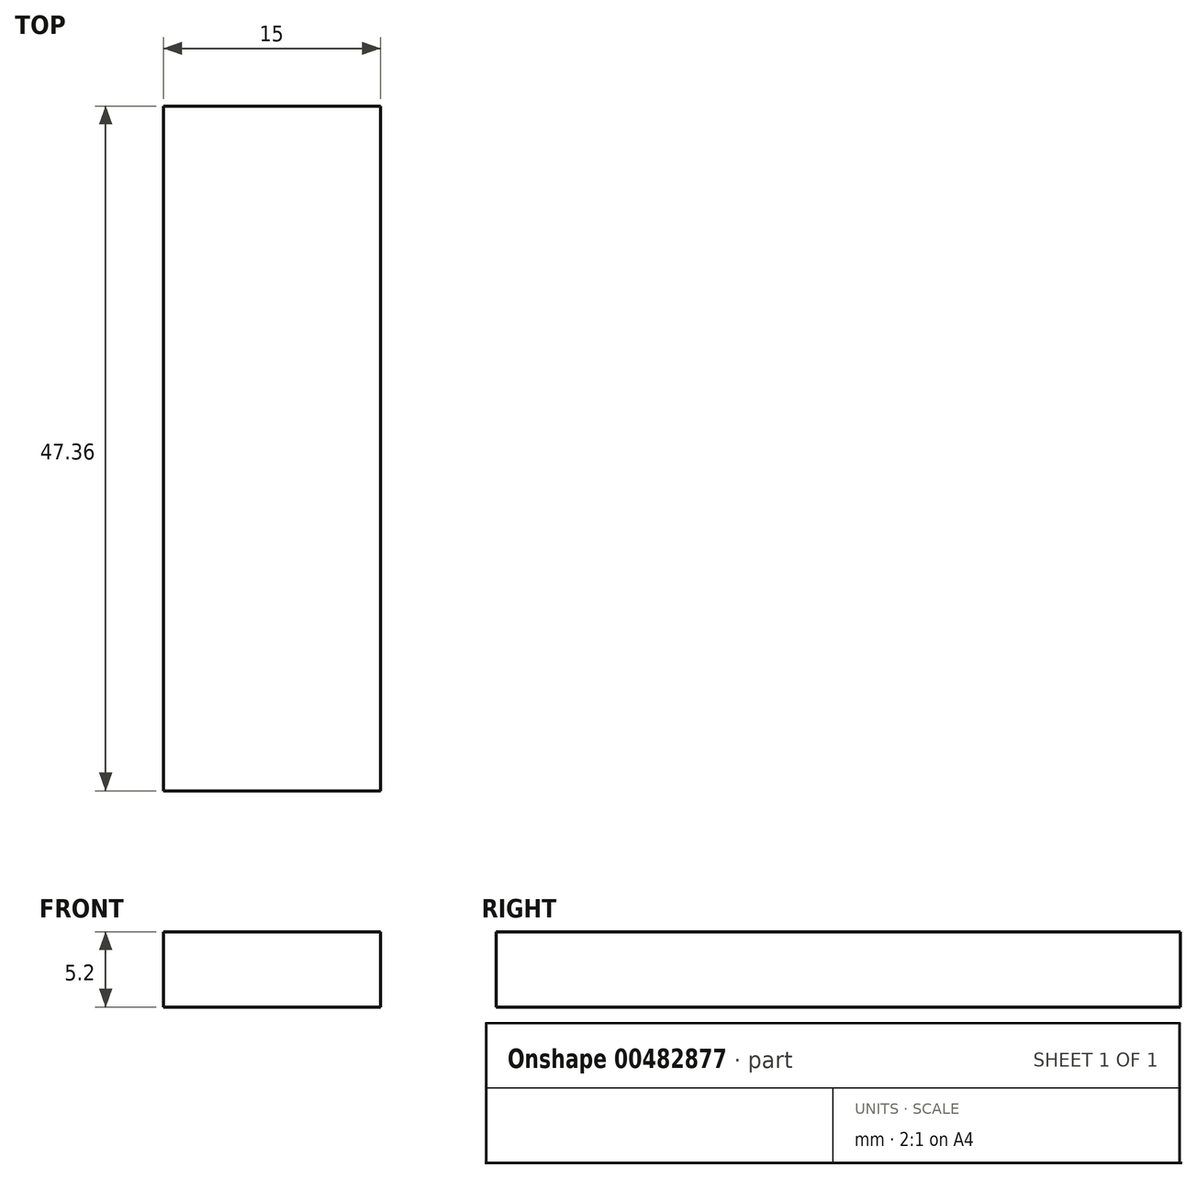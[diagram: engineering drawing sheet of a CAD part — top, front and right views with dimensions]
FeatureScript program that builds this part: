
annotation { "Feature Type Name" : "Feature", "Feature Type Description" : "" }
export const myFeature = defineFeature(function(context is Context, id is Id, definition is map)
    precondition{}
    {
        {
            var Q0;
            Q0=qCreatedBy(makeId("Top.planeOp"),FACE);
            var sketch = newSketch(context, id + "F0", { "sketchPlane" : qUnion([Q0])});
            skLineSegment(sketch, "E0.bottom", {"start": v(7.5, -23.68) * mm, "end": v(-7.5, -23.68) * mm});
            skLineSegment(sketch, "E0.top", {"start": v(7.5, 23.68) * mm, "end": v(-7.5, 23.68) * mm});
            skLineSegment(sketch, "E0.left", {"start": v(7.5, -23.68) * mm, "end": v(7.5, 23.68) * mm});
            skLineSegment(sketch, "E0.right", {"start": v(-7.5, -23.68) * mm, "end": v(-7.5, 23.68) * mm});
            skPoint(sketch, "E0.middle", {"position": v(0, 0) * mm});
            skSolve(sketch);
        }
        {
            var Q0;
            Q0=makeQuery(id+"F0.imprint","IMPRINT",FACE,{"disambiguationData":[TD([[makeQuery(id+"F0.imprint","IMPRINT",EDGE,{"derivedFrom":sQuery(id+"F0.wireOp",EDGE,"E0.bottom")}),-1.0]])]});
            extrude(context, id + "F1", {"entities" : qUnion([Q0]), "depth" : 5.2 * mm});
        }
        {
            var Q0;
            Q0=makeQuery(id+"F1.opExtrude","SWEPT_FACE",FACE,{"disambiguationData":[OSD([sQuery(id+"F0.wireOp",EDGE,"E0.right")])]});
            var sketch = newSketch(context, id + "F2", { "sketchPlane" : qUnion([Q0])});
            skCircle(sketch, "E1", {"center": v(-9.02, 2.6) * mm, "radius": 1.7 * mm});
            skLineSegment(sketch, "E2", {"start": v(0, 0) * mm, "end": v(0, 5.2) * mm, "construction": true});
            skCircle(sketch, "E3.MirrorC", {"center": v(9.02, 2.6) * mm, "radius": 1.7 * mm});
            skSolve(sketch);
        }
        {
            var Q0;
            Q0=sQuery(id+"F2.wireOp",EDGE,"E3.MirrorC");
            var Q1;
            Q1=sQuery(id+"F2.wireOp",EDGE,"E1");
            extrude(context, id + "F3", {"bodyType" : ToolBodyType.SURFACE, "surfaceEntities" : qUnion([Q0, Q1]), "depth" : 62 * mm});
        }
    });
